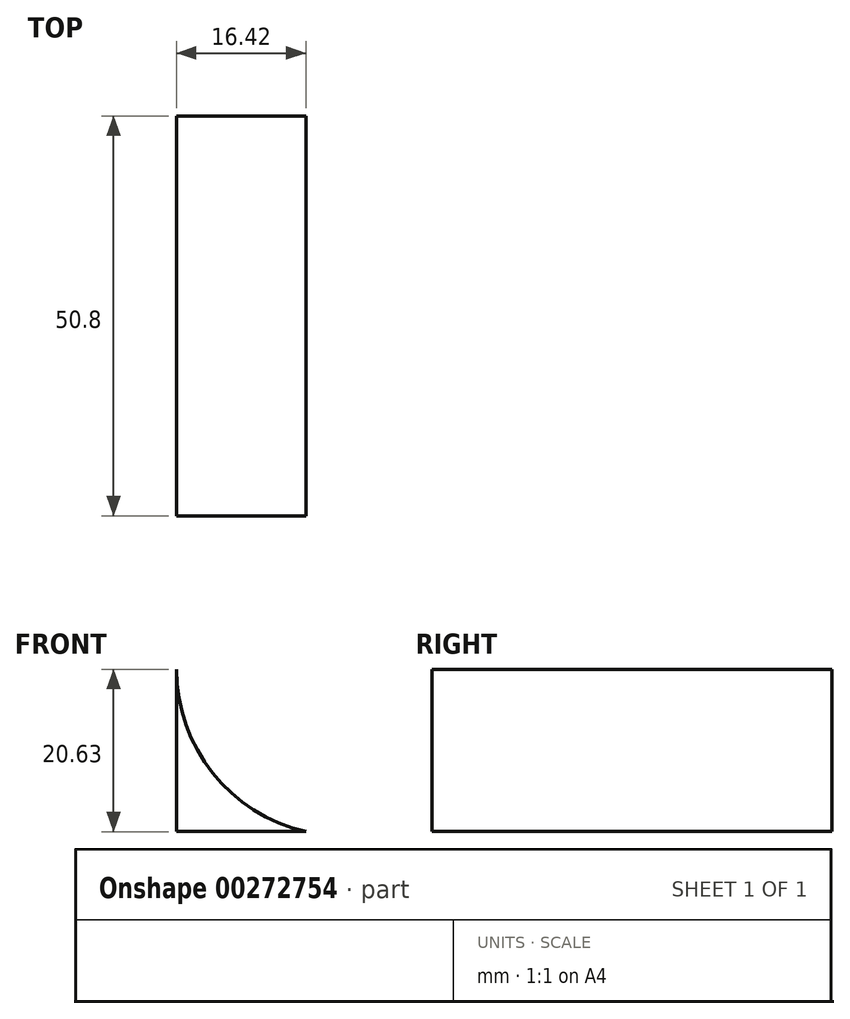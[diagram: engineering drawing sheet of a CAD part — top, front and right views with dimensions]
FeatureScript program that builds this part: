
annotation { "Feature Type Name" : "Feature", "Feature Type Description" : "" }
export const myFeature = defineFeature(function(context is Context, id is Id, definition is map)
    precondition{}
    {
        {
            var Q0;
            Q0=qCreatedBy(makeId("Front.planeOp"),FACE);
            var sketch = newSketch(context, id + "F0", { "sketchPlane" : qUnion([Q0])});
            skLineSegment(sketch, "E0", {"start": v(-58.81, 43.16) * mm, "end": v(-58.81, 0) * mm});
            skLineSegment(sketch, "E1", {"start": v(-58.81, 0) * mm, "end": v(-58.81, 43.16) * mm});
            skLineSegment(sketch, "E2", {"start": v(-58.81, 43.16) * mm, "end": v(-40.86, 43.16) * mm});
            skLineSegment(sketch, "E3", {"start": v(-40.86, 43.16) * mm, "end": v(-40.86, 22.53) * mm});
            skLineSegment(sketch, "E4", {"start": v(-40.86, 22.53) * mm, "end": v(-24.44, 22.53) * mm});
            skLineSegment(sketch, "E5", {"start": v(-24.44, 22.53) * mm, "end": v(-24.44, 0) * mm});
            skLineSegment(sketch, "E6", {"start": v(-24.44, 0) * mm, "end": v(-58.81, 0) * mm});
            skArc(sketch, "E7", {"start": v(-40.86, 43.16) * mm, "mid": v(-36.26, 29.97) * mm, "end": v(-24.44, 22.53) * mm});
            skSolve(sketch);
        }
        {
            var Q0;
            Q0=makeQuery(id+"F0.imprint","IMPRINT",FACE,{"disambiguationData":[TD([[makeQuery(id+"F0.imprint","IMPRINT",EDGE,{"derivedFrom":sQuery(id+"F0.wireOp",EDGE,"E3")}),1.0]])]});
            var Q1;
            Q1=makeQuery(id+"F0.imprint","IMPRINT",FACE,{"disambiguationData":[TD([[makeQuery(id+"F0.imprint","IMPRINT",EDGE,{"derivedFrom":sQuery(id+"F0.wireOp",EDGE,"E1")}),-1.0]])]});
            extrude(context, id + "F1", {"entities" : qUnion([Q0, Q1]), "depth" : 50.8 * mm});
        }
    });
